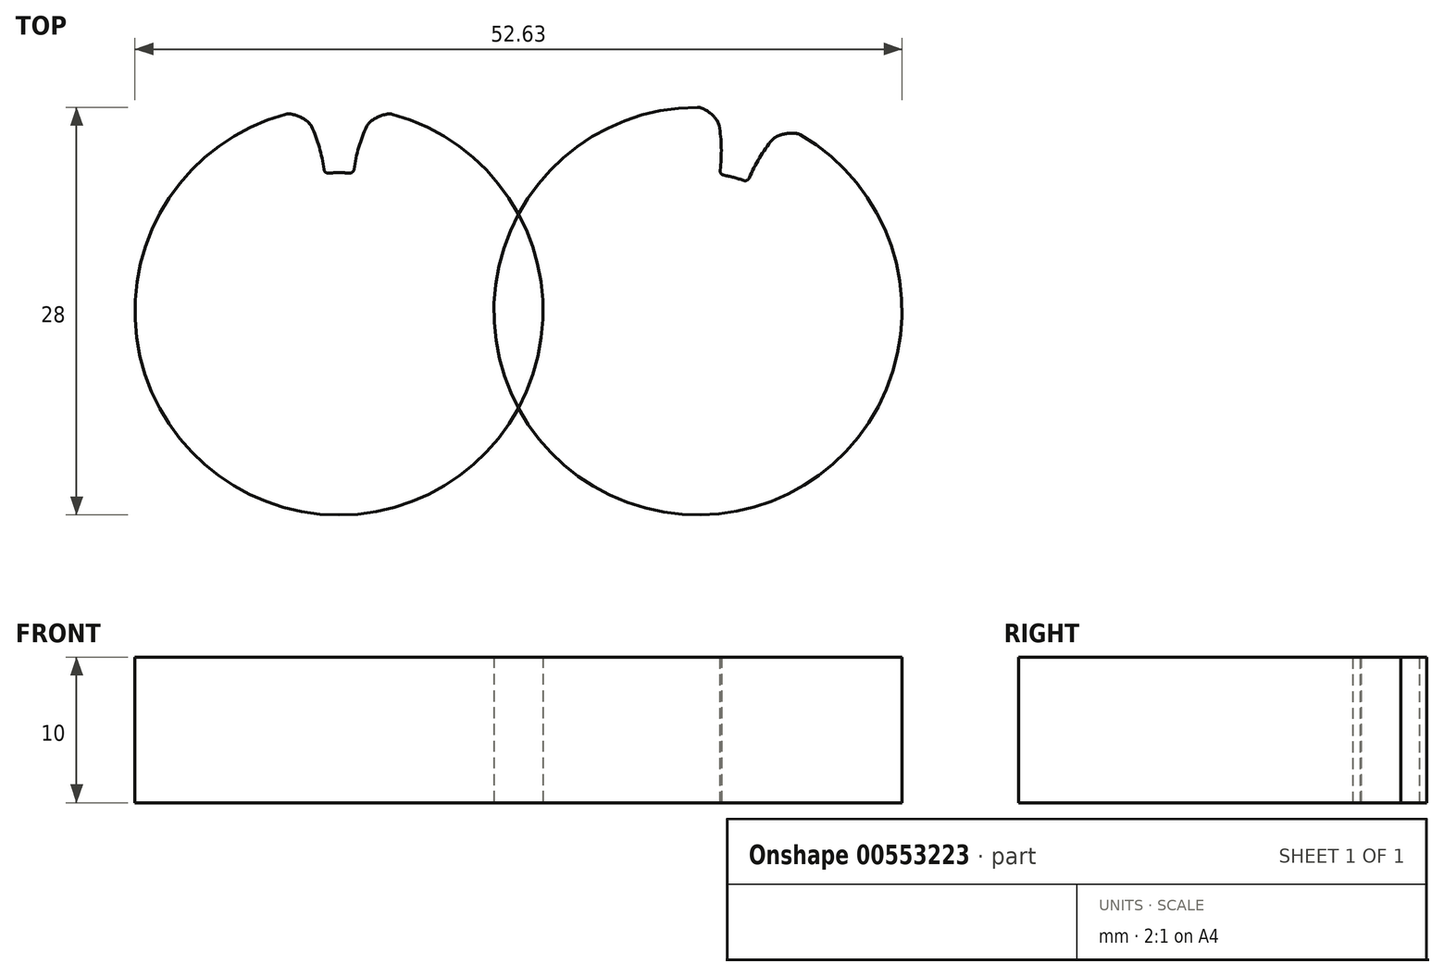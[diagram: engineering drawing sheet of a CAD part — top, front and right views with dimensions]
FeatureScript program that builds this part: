
annotation { "Feature Type Name" : "Feature", "Feature Type Description" : "" }
export const myFeature = defineFeature(function(context is Context, id is Id, definition is map)
    precondition{}
    {
        {
            var Q0;
            Q0=qCreatedBy(makeId("Top.planeOp"),FACE);
            var sketch = newSketch(context, id + "F0", { "sketchPlane" : qUnion([Q0])});
            skCircle(sketch, "E0", {"center": v(0, 0) * mm, "radius": 9.5 * mm});
            skCircle(sketch, "E1", {"center": v(0, 0) * mm, "radius": 14 * mm});
            skCircle(sketch, "E2", {"center": v(0, 0) * mm, "radius": 12 * mm, "construction": true});
            skArc(sketch, "E3", {"start": v(-1, 9.45) * mm, "mid": v(-1.73, 12.32) * mm, "end": v(-3.25, 14.87) * mm});
            skArc(sketch, "E4.MirrorCS", {"start": v(1, 9.45) * mm, "mid": v(1.73, 12.32) * mm, "end": v(3.25, 14.87) * mm});
            skArc(sketch, "E5", {"start": v(3.25, 14.87) * mm, "mid": v(0, 15.22) * mm, "end": v(-3.25, 14.87) * mm});
            skLineSegment(sketch, "E6", {"start": v(-1, 9.45) * mm, "end": v(0, 0) * mm, "construction": true});
            skLineSegment(sketch, "E7", {"start": v(-1.57, 11.9) * mm, "end": v(1.57, 11.9) * mm, "construction": true});
            skLineSegment(sketch, "E8", {"start": v(-1.57, 11.9) * mm, "end": v(0, 7.6) * mm, "construction": true});
            skPoint(sketch, "E8.endSnap0", {"position": v(0, 11.9) * mm});
            skLineSegment(sketch, "E9", {"start": v(1.57, 11.9) * mm, "end": v(4.6, 11.09) * mm, "construction": true});
            skLineSegment(sketch, "E10", {"start": v(0, 0) * mm, "end": v(4.28, 15.96) * mm, "construction": true});
            skSolve(sketch);
        }
        {
            var Q0;
            {var subQ0=sQuery(id+"F0.wireOp",EDGE,"E3");var subQ1=sQuery(id+"F0.wireOp",EDGE,"E0");var subQ2=makeQuery(id+"F0.imprint","INTERSECT",VERTEX,{"derivedFrom":[subQ1,subQ0]});Q0=makeQuery(id+"F0.imprint","IMPRINT",FACE,{"disambiguationData":[TD([[makeQuery(id+"F0.imprint","IMPRINT",EDGE,{"disambiguationData":[TD([[subQ2,-1.0]])],"derivedFrom":subQ1}),-1.0]])]});}
            var Q1;
            {var subQ0=sQuery(id+"F0.wireOp",EDGE,"E0");var subQ1=makeQuery(id+"F0.imprint","INTERSECT",VERTEX,{"derivedFrom":[subQ0,sQuery(id+"F0.wireOp",EDGE,"E3")]});Q1=makeQuery(id+"F0.imprint","IMPRINT",FACE,{"disambiguationData":[TD([[makeQuery(id+"F0.imprint","IMPRINT",EDGE,{"disambiguationData":[TD([[subQ1,1.0]])],"derivedFrom":subQ0}),1.0]])]});}
            var Q2;
            {var subQ0=sQuery(id+"F0.wireOp",EDGE,"E3");var subQ1=sQuery(id+"F0.wireOp",EDGE,"E0");var subQ2=makeQuery(id+"F0.imprint","INTERSECT",VERTEX,{"derivedFrom":[subQ1,subQ0]});Q2=makeQuery(id+"F0.imprint","IMPRINT",FACE,{"disambiguationData":[TD([[makeQuery(id+"F0.imprint","IMPRINT",EDGE,{"disambiguationData":[TD([[subQ2,1.0]])],"derivedFrom":subQ1}),-1.0]])]});}
            extrude(context, id + "F1", {"entities" : qUnion([Q0, Q1, Q2]), "depth" : 10 * mm, "offsetDistance" : 25 * mm});
        }
        {
            var Q0;
            {var subQ0=sQuery(id+"F0.wireOp",EDGE,"E3");var subQ1=sQuery(id+"F0.wireOp",EDGE,"E0");var subQ2=makeQuery(id+"F0.imprint","INTERSECT",VERTEX,{"derivedFrom":[subQ1,subQ0]});Q0=makeQuery(id+"F0.imprint","IMPRINT",FACE,{"disambiguationData":[TD([[makeQuery(id+"F0.imprint","IMPRINT",EDGE,{"disambiguationData":[TD([[subQ2,1.0]])],"derivedFrom":subQ1}),-1.0]])]});}
            var Q1;
            {var subQ5=sQuery(id+"F0.wireOp",EDGE,"E5");Q1=makeQuery(id+"F0.imprint","IMPRINT",FACE,{"disambiguationData":[TD([[makeQuery(id+"F0.imprint","IMPRINT",EDGE,{"derivedFrom":subQ5}),1.0]])]});}
            extrude(context, id + "F2", {"entities" : qUnion([Q0, Q1]), "operationType" : NewBodyOperationType.REMOVE, "depth" : 10 * mm, "offsetDistance" : 25 * mm});
        }
        {
            var Q0;
            Q0=makeQuery(id+"F2.boolean.opBoolean","INTERSECT",EDGE,{"derivedFrom":[makeQuery(id+"F1.opExtrude","SWEPT_FACE",FACE,{"disambiguationData":[OSD([sQuery(id+"F0.wireOp",EDGE,"E1")])]}),makeQuery(id+"F2.opExtrude","SWEPT_FACE",FACE,{"disambiguationData":[OSD([sQuery(id+"F0.wireOp",EDGE,"E3")])]})]});
            var Q1;
            Q1=makeQuery(id+"F2.boolean.opBoolean","INTERSECT",EDGE,{"derivedFrom":[makeQuery(id+"F1.opExtrude","SWEPT_FACE",FACE,{"disambiguationData":[OSD([sQuery(id+"F0.wireOp",EDGE,"E1")])]}),makeQuery(id+"F2.opExtrude","SWEPT_FACE",FACE,{"disambiguationData":[OSD([sQuery(id+"F0.wireOp",EDGE,"E4.MirrorCS")])]})]});
            fillet(context, id + "F3", {"entities" : qUnion([Q0, Q1]), "radius" : 1.5 * mm, "tangentPropagation" : true, "rho" : .3, "crossSection" : FilletCrossSection.CONIC, "allowEdgeOverflow" : false});
        }
        {
            var Q0;
            Q0=makeQuery(id+"F2.boolean.opBoolean","COPY",EDGE,{"derivedFrom":makeQuery(id+"F2.opExtrude","SWEPT_EDGE",EDGE,{"disambiguationData":[OSD([sQuery(id+"F0.wireOp",EDGE,"E0"),sQuery(id+"F0.wireOp",EDGE,"E3")])]})});
            var Q1;
            Q1=makeQuery(id+"F2.boolean.opBoolean","COPY",EDGE,{"derivedFrom":makeQuery(id+"F2.opExtrude","SWEPT_EDGE",EDGE,{"disambiguationData":[OSD([sQuery(id+"F0.wireOp",EDGE,"E0"),sQuery(id+"F0.wireOp",EDGE,"E4.MirrorCS")])]})});
            fillet(context, id + "F4", {"entities" : qUnion([Q0, Q1]), "radius" : .3 * mm, "tangentPropagation" : true, "allowEdgeOverflow" : false});
        }
        {
            var Q0;
            Q0=makeQuery(id+"F1.opExtrude","SWEPT_BODY",BODY,{"disambiguationData":[OSD([sQuery(id+"F0.wireOp",EDGE,"E1")])]});
            var Q1;
            {var subQ0=sQuery(id+"F0.wireOp",EDGE,"E1");var subQ3=sQuery(id+"F0.wireOp",EDGE,"E4.MirrorCS");var subQ4=sQuery(id+"F0.wireOp",EDGE,"E3");Q1=makeQuery(id+"FbKghmHJUCrtXIK_1.2.F2.boolean.opBoolean","SPLIT",FACE,{"disambiguationData":[TD([makeQuery(id+"FbKghmHJUCrtXIK_1.2.F2.opExtrude","SWEPT_FACE",FACE,{"disambiguationData":[OSD([subQ4])]})])],"derivedFrom":makeQuery(id+"FbKghmHJUCrtXIK_1.1.F2.boolean.opBoolean","SPLIT",FACE,{"disambiguationData":[TD([makeQuery(id+"FbKghmHJUCrtXIK_1.1.F2.opExtrude","SWEPT_FACE",FACE,{"disambiguationData":[OSD([subQ3])]})])],"derivedFrom":makeQuery(id+"F1.opExtrude","SWEPT_FACE",FACE,{"disambiguationData":[OSD([subQ0])]})})});}
            transform(context, id + "F5", {"entities" : qUnion([Q0]), "transformType" : TransformType.ROTATION, "transformAxis" : qUnion([Q1]), "angle" : 15 * degree, "makeCopy" : true});
        }
        {
            var Q0;
            Q0=makeQuery(id+"F5.opPattern","COPY",BODY,{"derivedFrom":makeQuery(id+"F1.opExtrude","SWEPT_BODY",BODY,{"disambiguationData":[OSD([sQuery(id+"F0.wireOp",EDGE,"E1")])]}),"instanceName":"1"});
            transform(context, id + "F6", {"entities" : qUnion([Q0]), "transformType" : TransformType.TRANSLATION_3D, "dx" : 24.62 * mm, "dy" : 0 * mm, "dz" : 0 * mm, "makeCopy" : false});
        }
    });
